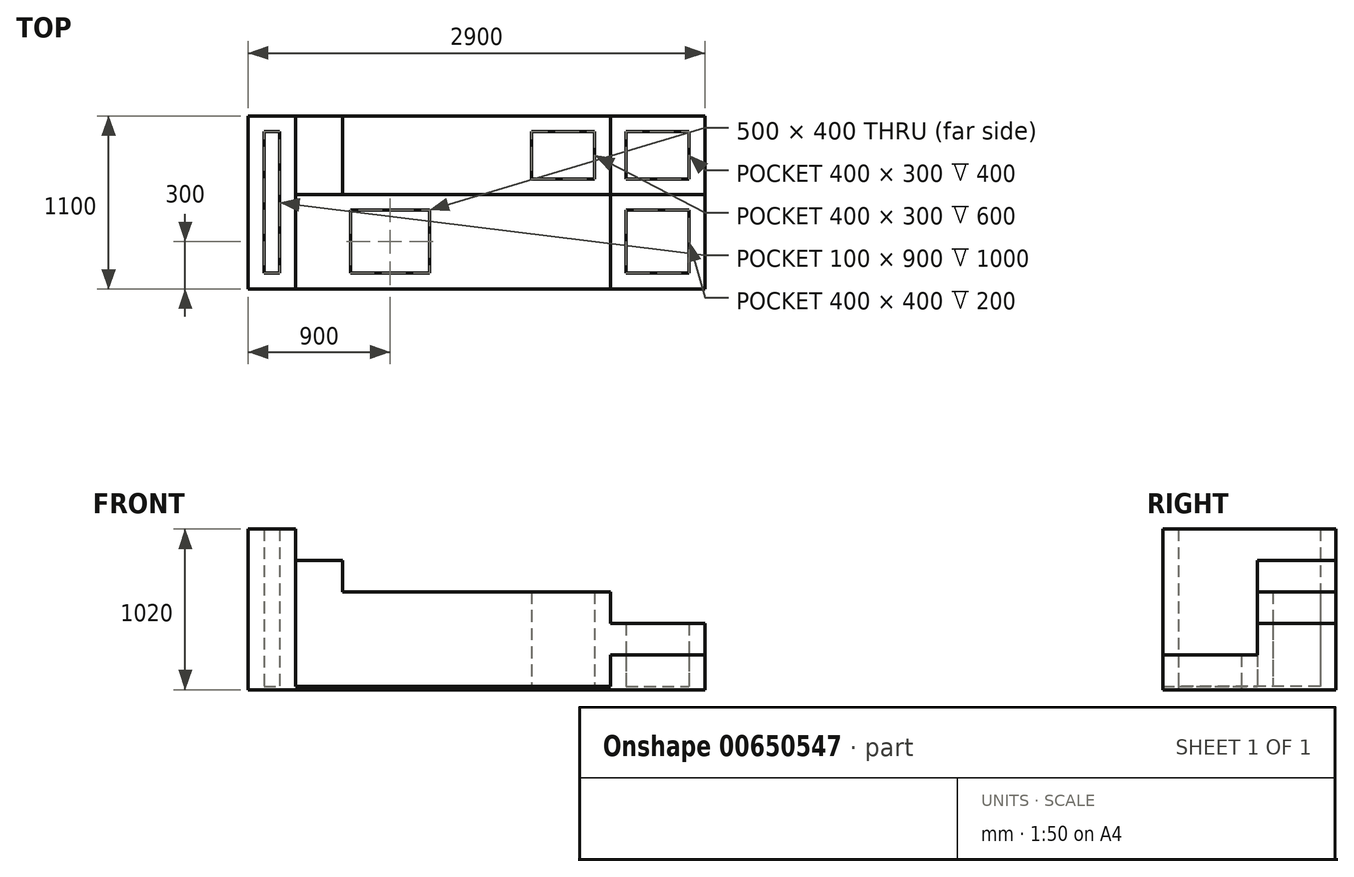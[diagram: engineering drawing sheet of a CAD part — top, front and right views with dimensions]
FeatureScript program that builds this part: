
annotation { "Feature Type Name" : "Feature", "Feature Type Description" : "" }
export const myFeature = defineFeature(function(context is Context, id is Id, definition is map)
    precondition{}
    {
        {
            var Q0;
            Q0=qCreatedBy(makeId("Top.planeOp"),FACE);
            var sketch = newSketch(context, id + "F0", { "sketchPlane" : qUnion([Q0])});
            skLineSegment(sketch, "E0.bottom", {"start": v(0, 0) * mm, "end": v(-2350, 0) * mm});
            skLineSegment(sketch, "E0.top", {"start": v(0, 1100) * mm, "end": v(-2900, 1100) * mm});
            skLineSegment(sketch, "E0.left", {"start": v(0, 0) * mm, "end": v(0, 1100) * mm});
            skLineSegment(sketch, "E0.right", {"start": v(-2900, 0) * mm, "end": v(-2900, 1100) * mm});
            skLineSegment(sketch, "E1.bottom", {"start": v(-1750, 100) * mm, "end": v(-2250, 100) * mm});
            skLineSegment(sketch, "E1.top", {"start": v(-1750, 500) * mm, "end": v(-2250, 500) * mm});
            skLineSegment(sketch, "E1.left", {"start": v(-1750, 100) * mm, "end": v(-1750, 500) * mm});
            skLineSegment(sketch, "E1.right", {"start": v(-2250, 100) * mm, "end": v(-2250, 500) * mm});
            skLineSegment(sketch, "E2", {"start": v(-2350, 0) * mm, "end": v(-2900, 0) * mm});
            skSolve(sketch);
        }
        {
            var Q0;
            Q0=makeQuery(id+"F0.imprint","IMPRINT",FACE,{"disambiguationData":[TD([[makeQuery(id+"F0.imprint","IMPRINT",EDGE,{"derivedFrom":sQuery(id+"F0.wireOp",EDGE,"E0.bottom")}),-1.0]])]});
            extrude(context, id + "F1", {"entities" : qUnion([Q0]), "depth" : 20 * mm, "offsetDistance" : 25 * mm});
        }
        {
            var Q0;
            Q0=makeQuery(id+"F1.opExtrude","CAP_FACE",FACE,{"disambiguationData":[OSD([sQuery(id+"F0.wireOp",EDGE,"E0.bottom"),sQuery(id+"F0.wireOp",EDGE,"E0.top"),sQuery(id+"F0.wireOp",EDGE,"E0.left"),sQuery(id+"F0.wireOp",EDGE,"E0.right"),sQuery(id+"F0.wireOp",EDGE,"E1.bottom"),sQuery(id+"F0.wireOp",EDGE,"E1.top"),sQuery(id+"F0.wireOp",EDGE,"E1.left"),sQuery(id+"F0.wireOp",EDGE,"E1.right")])],"isStart":false});
            var sketch = newSketch(context, id + "F2", { "sketchPlane" : qUnion([Q0])});
            skLineSegment(sketch, "E3.bottom", {"start": v(0, 1100) * mm, "end": v(-600, 1100) * mm});
            skLineSegment(sketch, "E3.top", {"start": v(0, 600) * mm, "end": v(-600, 600) * mm});
            skLineSegment(sketch, "E3.left", {"start": v(0, 1100) * mm, "end": v(0, 600) * mm});
            skLineSegment(sketch, "E3.right", {"start": v(-600, 1100) * mm, "end": v(-600, 600) * mm});
            skLineSegment(sketch, "E4.bottom", {"start": v(-500, 1000) * mm, "end": v(-100, 1000) * mm});
            skLineSegment(sketch, "E4.top", {"start": v(-500, 700) * mm, "end": v(-100, 700) * mm});
            skLineSegment(sketch, "E4.left", {"start": v(-500, 1000) * mm, "end": v(-500, 700) * mm});
            skLineSegment(sketch, "E4.right", {"start": v(-100, 1000) * mm, "end": v(-100, 700) * mm});
            skSolve(sketch);
        }
        {
            var Q0;
            Q0=qSketchRegion(id+"F2",true);
            extrude(context, id + "F3", {"entities" : qUnion([Q0]), "operationType" : NewBodyOperationType.ADD, "depth" : 400 * mm, "offsetDistance" : 25 * mm});
        }
        {
            var Q0;
            {var subQ0=sQuery(id+"F0.wireOp",EDGE,"E0.left");var subQ1=sQuery(id+"F0.wireOp",EDGE,"E1.right");var subQ2=sQuery(id+"F0.wireOp",EDGE,"E1.left");var subQ3=sQuery(id+"F0.wireOp",EDGE,"E1.top");var subQ4=sQuery(id+"F0.wireOp",EDGE,"E1.bottom");var subQ5=sQuery(id+"F0.wireOp",EDGE,"E0.bottom");var subQ6=sQuery(id+"F0.wireOp",EDGE,"E0.right");var subQ7=sQuery(id+"F0.wireOp",EDGE,"E0.top");Q0=makeQuery(id+"F3.boolean.opBoolean","SPLIT",FACE,{"disambiguationData":[TD([makeQuery(id+"F1.opExtrude","SWEPT_FACE",FACE,{"disambiguationData":[OSD([subQ5])]})])],"derivedFrom":makeQuery(id+"F1.opExtrude","CAP_FACE",FACE,{"disambiguationData":[OSD([subQ5,subQ7,subQ0,subQ6,subQ4,subQ3,subQ2,subQ1])],"isStart":false})});}
            var sketch = newSketch(context, id + "F4", { "sketchPlane" : qUnion([Q0])});
            skLineSegment(sketch, "E5.bottom", {"start": v(-600, 600) * mm, "end": v(-2300, 600) * mm});
            skLineSegment(sketch, "E5.top", {"start": v(-600, 1100) * mm, "end": v(-2300, 1100) * mm});
            skLineSegment(sketch, "E5.left", {"start": v(-600, 600) * mm, "end": v(-600, 1100) * mm});
            skLineSegment(sketch, "E5.right", {"start": v(-2300, 600) * mm, "end": v(-2300, 1100) * mm});
            skLineSegment(sketch, "E6.bottom", {"start": v(-700, 700) * mm, "end": v(-1100, 700) * mm});
            skLineSegment(sketch, "E6.top", {"start": v(-700, 1000) * mm, "end": v(-1100, 1000) * mm});
            skLineSegment(sketch, "E6.left", {"start": v(-700, 700) * mm, "end": v(-700, 1000) * mm});
            skLineSegment(sketch, "E6.right", {"start": v(-1100, 700) * mm, "end": v(-1100, 1000) * mm});
            skSolve(sketch);
        }
        {
            var Q0;
            Q0=qSketchRegion(id+"F4",true);
            extrude(context, id + "F5", {"entities" : qUnion([Q0]), "operationType" : NewBodyOperationType.ADD, "depth" : 600 * mm, "offsetDistance" : 25 * mm});
        }
        {
            var Q0;
            {var subQ1=sQuery(id+"F0.wireOp",EDGE,"E0.left");var subQ3=sQuery(id+"F0.wireOp",EDGE,"E1.right");var subQ5=sQuery(id+"F0.wireOp",EDGE,"E1.left");var subQ8=sQuery(id+"F0.wireOp",EDGE,"E1.top");var subQ11=sQuery(id+"F0.wireOp",EDGE,"E1.bottom");var subQ13=sQuery(id+"F0.wireOp",EDGE,"E0.bottom");var subQ14=makeQuery(id+"F1.opExtrude","SWEPT_FACE",FACE,{"disambiguationData":[OSD([subQ13])]});var subQ15=sQuery(id+"F0.wireOp",EDGE,"E0.right");var subQ17=sQuery(id+"F0.wireOp",EDGE,"E0.top");Q0=makeQuery(id+"F5.boolean.opBoolean","SPLIT",FACE,{"disambiguationData":[TD([subQ14])],"derivedFrom":makeQuery(id+"F3.boolean.opBoolean","SPLIT",FACE,{"disambiguationData":[TD([subQ14])],"derivedFrom":makeQuery(id+"F1.opExtrude","CAP_FACE",FACE,{"disambiguationData":[OSD([subQ13,subQ17,subQ1,subQ15,subQ11,subQ8,subQ5,subQ3])],"isStart":false})})});}
            var sketch = newSketch(context, id + "F6", { "sketchPlane" : qUnion([Q0])});
            skLineSegment(sketch, "E7.bottom", {"start": v(-2300, 600) * mm, "end": v(-2600, 600) * mm});
            skLineSegment(sketch, "E7.top", {"start": v(-2300, 1100) * mm, "end": v(-2600, 1100) * mm});
            skLineSegment(sketch, "E7.left", {"start": v(-2300, 600) * mm, "end": v(-2300, 1100) * mm});
            skLineSegment(sketch, "E7.right", {"start": v(-2600, 600) * mm, "end": v(-2600, 1100) * mm});
            skSolve(sketch);
        }
        {
            var Q0;
            Q0=qSketchRegion(id+"F6",true);
            extrude(context, id + "F7", {"entities" : qUnion([Q0]), "operationType" : NewBodyOperationType.ADD, "depth" : 800 * mm, "offsetDistance" : 25 * mm});
        }
        {
            var Q0;
            {var subQ1=sQuery(id+"F0.wireOp",EDGE,"E0.left");var subQ3=sQuery(id+"F0.wireOp",EDGE,"E1.right");var subQ5=sQuery(id+"F0.wireOp",EDGE,"E1.left");var subQ8=sQuery(id+"F0.wireOp",EDGE,"E1.top");var subQ11=sQuery(id+"F0.wireOp",EDGE,"E1.bottom");var subQ13=sQuery(id+"F0.wireOp",EDGE,"E0.bottom");var subQ14=makeQuery(id+"F1.opExtrude","SWEPT_FACE",FACE,{"disambiguationData":[OSD([subQ13])]});var subQ15=sQuery(id+"F0.wireOp",EDGE,"E0.right");var subQ17=sQuery(id+"F0.wireOp",EDGE,"E0.top");Q0=makeQuery(id+"F7.boolean.opBoolean","SPLIT",FACE,{"disambiguationData":[TD([subQ14])],"derivedFrom":makeQuery(id+"F5.boolean.opBoolean","SPLIT",FACE,{"disambiguationData":[TD([subQ14])],"derivedFrom":makeQuery(id+"F3.boolean.opBoolean","SPLIT",FACE,{"disambiguationData":[TD([subQ14])],"derivedFrom":makeQuery(id+"F1.opExtrude","CAP_FACE",FACE,{"disambiguationData":[OSD([subQ13,subQ17,subQ1,subQ15,subQ11,subQ8,subQ5,subQ3])],"isStart":false})})})});}
            var sketch = newSketch(context, id + "F8", { "sketchPlane" : qUnion([Q0])});
            skLineSegment(sketch, "E8.bottom", {"start": v(-2900, 1100) * mm, "end": v(-2600, 1100) * mm});
            skLineSegment(sketch, "E8.top", {"start": v(-2900, 0) * mm, "end": v(-2600, 0) * mm});
            skLineSegment(sketch, "E8.left", {"start": v(-2900, 1100) * mm, "end": v(-2900, 0) * mm});
            skLineSegment(sketch, "E8.right", {"start": v(-2600, 1100) * mm, "end": v(-2600, 0) * mm});
            skLineSegment(sketch, "E9.bottom", {"start": v(-2800, 1000) * mm, "end": v(-2700, 1000) * mm});
            skLineSegment(sketch, "E9.top", {"start": v(-2800, 100) * mm, "end": v(-2700, 100) * mm});
            skLineSegment(sketch, "E9.left", {"start": v(-2800, 1000) * mm, "end": v(-2800, 100) * mm});
            skLineSegment(sketch, "E9.right", {"start": v(-2700, 1000) * mm, "end": v(-2700, 100) * mm});
            skSolve(sketch);
        }
        {
            var Q0;
            Q0=qSketchRegion(id+"F8",true);
            extrude(context, id + "F9", {"entities" : qUnion([Q0]), "operationType" : NewBodyOperationType.ADD, "depth" : 1000 * mm, "offsetDistance" : 25 * mm});
        }
        {
            var Q0;
            {var subQ1=sQuery(id+"F0.wireOp",EDGE,"E1.top");var subQ5=sQuery(id+"F0.wireOp",EDGE,"E1.left");var subQ7=sQuery(id+"F0.wireOp",EDGE,"E1.right");var subQ9=sQuery(id+"F0.wireOp",EDGE,"E2");var subQ10=sQuery(id+"F0.wireOp",EDGE,"E0.bottom");var subQ12=sQuery(id+"F0.wireOp",EDGE,"E0.left");var subQ13=makeQuery(id+"F1.opExtrude","SWEPT_FACE",FACE,{"disambiguationData":[OSD([subQ12])]});var subQ15=sQuery(id+"F0.wireOp",EDGE,"E1.bottom");var subQ18=sQuery(id+"F0.wireOp",EDGE,"E0.top");var subQ19=makeQuery(id+"F1.opExtrude","SWEPT_FACE",FACE,{"disambiguationData":[OSD([subQ18])]});var subQ20=sQuery(id+"F0.wireOp",EDGE,"E0.right");Q0=makeQuery(id+"F9.boolean.opBoolean","SPLIT",FACE,{"disambiguationData":[TD([subQ13])],"derivedFrom":makeQuery(id+"F7.boolean.opBoolean","SPLIT",FACE,{"disambiguationData":[TD([subQ19])],"derivedFrom":makeQuery(id+"F5.boolean.opBoolean","SPLIT",FACE,{"disambiguationData":[TD([subQ19])],"derivedFrom":makeQuery(id+"F3.boolean.opBoolean","SPLIT",FACE,{"disambiguationData":[TD([subQ19])],"derivedFrom":makeQuery(id+"F1.opExtrude","CAP_FACE",FACE,{"disambiguationData":[OSD([subQ10,subQ18,subQ12,subQ20,subQ15,subQ1,subQ5,subQ7,subQ9])],"isStart":false})})})})});}
            var sketch = newSketch(context, id + "F10", { "sketchPlane" : qUnion([Q0])});
            skLineSegment(sketch, "E10.bottom", {"start": v(0, 0) * mm, "end": v(-600, 0) * mm});
            skLineSegment(sketch, "E10.top", {"start": v(0, 600) * mm, "end": v(-600, 600) * mm});
            skLineSegment(sketch, "E10.left", {"start": v(0, 0) * mm, "end": v(0, 600) * mm});
            skLineSegment(sketch, "E10.right", {"start": v(-600, 0) * mm, "end": v(-600, 600) * mm});
            skLineSegment(sketch, "E11.bottom", {"start": v(-100, 100) * mm, "end": v(-500, 100) * mm});
            skLineSegment(sketch, "E11.top", {"start": v(-100, 500) * mm, "end": v(-500, 500) * mm});
            skLineSegment(sketch, "E11.left", {"start": v(-100, 100) * mm, "end": v(-100, 500) * mm});
            skLineSegment(sketch, "E11.right", {"start": v(-500, 100) * mm, "end": v(-500, 500) * mm});
            skSolve(sketch);
        }
        {
            var Q0;
            Q0=qSketchRegion(id+"F10",true);
            extrude(context, id + "F11", {"entities" : qUnion([Q0]), "operationType" : NewBodyOperationType.ADD, "depth" : 200 * mm, "offsetDistance" : 25 * mm});
        }
    });
